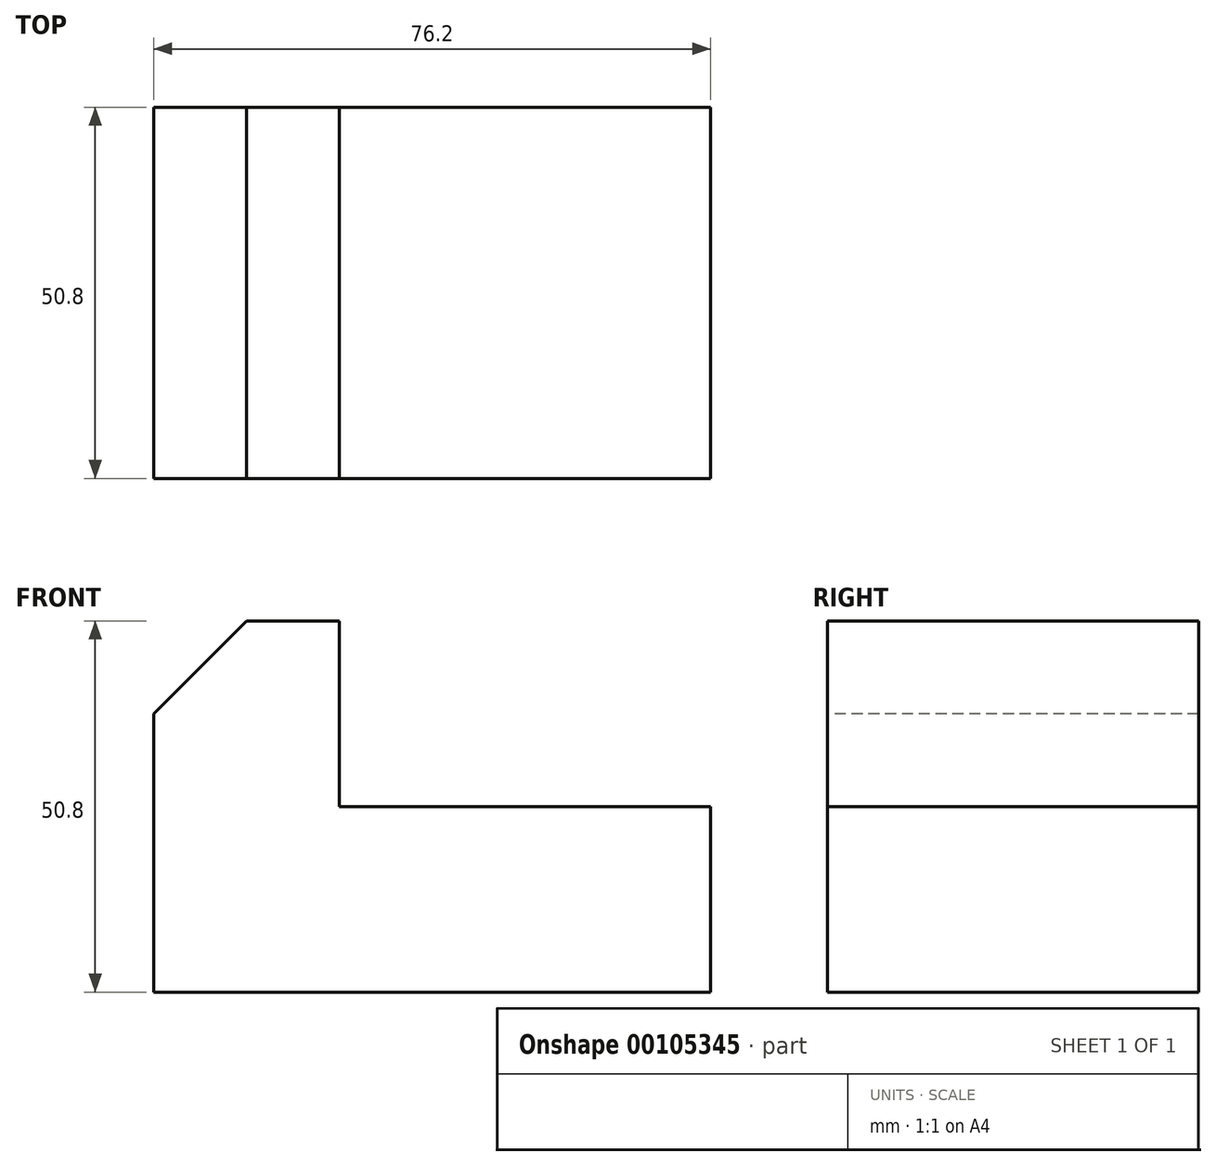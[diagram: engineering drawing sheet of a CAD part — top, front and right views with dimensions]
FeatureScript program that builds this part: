
annotation { "Feature Type Name" : "Feature", "Feature Type Description" : "" }
export const myFeature = defineFeature(function(context is Context, id is Id, definition is map)
    precondition{}
    {
        {
            var Q0;
            Q0=qCreatedBy(makeId("Front.planeOp"),FACE);
            var sketch = newSketch(context, id + "F0", { "sketchPlane" : qUnion([Q0])});
            skLineSegment(sketch, "E0.bottom", {"start": v(0, 0) * mm, "end": v(76.2, 0) * mm});
            skLineSegment(sketch, "E0.top", {"start": v(0, 50.8) * mm, "end": v(76.2, 50.8) * mm});
            skLineSegment(sketch, "E0.left", {"start": v(0, 0) * mm, "end": v(0, 50.8) * mm});
            skLineSegment(sketch, "E0.right", {"start": v(76.2, 0) * mm, "end": v(76.2, 50.8) * mm});
            skSolve(sketch);
        }
        {
            var Q0;
            Q0 = qSketchRegion(id + "F0", true);
            extrude(context, id + "F1", {"entities" : qUnion([Q0]), "endBound" : BoundingType.SYMMETRIC, "depth" : 50.8 * mm});
        }
        {
            var Q0;
            Q0=qCreatedBy(makeId("Front.planeOp"),FACE);
            var sketch = newSketch(context, id + "F2", { "sketchPlane" : qUnion([Q0])});
            skLineSegment(sketch, "E1", {"start": v(0, 38.1) * mm, "end": v(12.7, 50.8) * mm});
            skLineSegment(sketch, "E2", {"start": v(12.7, 50.8) * mm, "end": v(0, 50.8) * mm});
            skLineSegment(sketch, "E3", {"start": v(0, 50.8) * mm, "end": v(0, 38.1) * mm});
            skSolve(sketch);
        }
        {
            var Q0;
            Q0 = qSketchRegion(id + "F2", true);
            extrude(context, id + "F3", {"entities" : qUnion([Q0]), "operationType" : NewBodyOperationType.REMOVE, "endBound" : BoundingType.SYMMETRIC, "oppositeDirection" : true, "depth" : 50.8 * mm});
        }
        {
            var Q0;
            Q0=qCreatedBy(makeId("Front.planeOp"),FACE);
            var sketch = newSketch(context, id + "F4", { "sketchPlane" : qUnion([Q0])});
            skLineSegment(sketch, "E4.bottom", {"start": v(25.4, 50.8) * mm, "end": v(76.2, 50.8) * mm});
            skLineSegment(sketch, "E4.top", {"start": v(25.4, 25.4) * mm, "end": v(76.2, 25.4) * mm});
            skLineSegment(sketch, "E4.left", {"start": v(25.4, 50.8) * mm, "end": v(25.4, 25.4) * mm});
            skLineSegment(sketch, "E4.right", {"start": v(76.2, 50.8) * mm, "end": v(76.2, 25.4) * mm});
            skSolve(sketch);
        }
        {
            var Q0;
            Q0 = qSketchRegion(id + "F4", true);
            extrude(context, id + "F5", {"entities" : qUnion([Q0]), "operationType" : NewBodyOperationType.REMOVE, "endBound" : BoundingType.UP_TO_NEXT, "depth" : 91.74 * mm, "hasSecondDirection" : true, "secondDirectionOppositeDirection" : true, "secondDirectionDepth" : 87.34 * mm});
        }
    });
